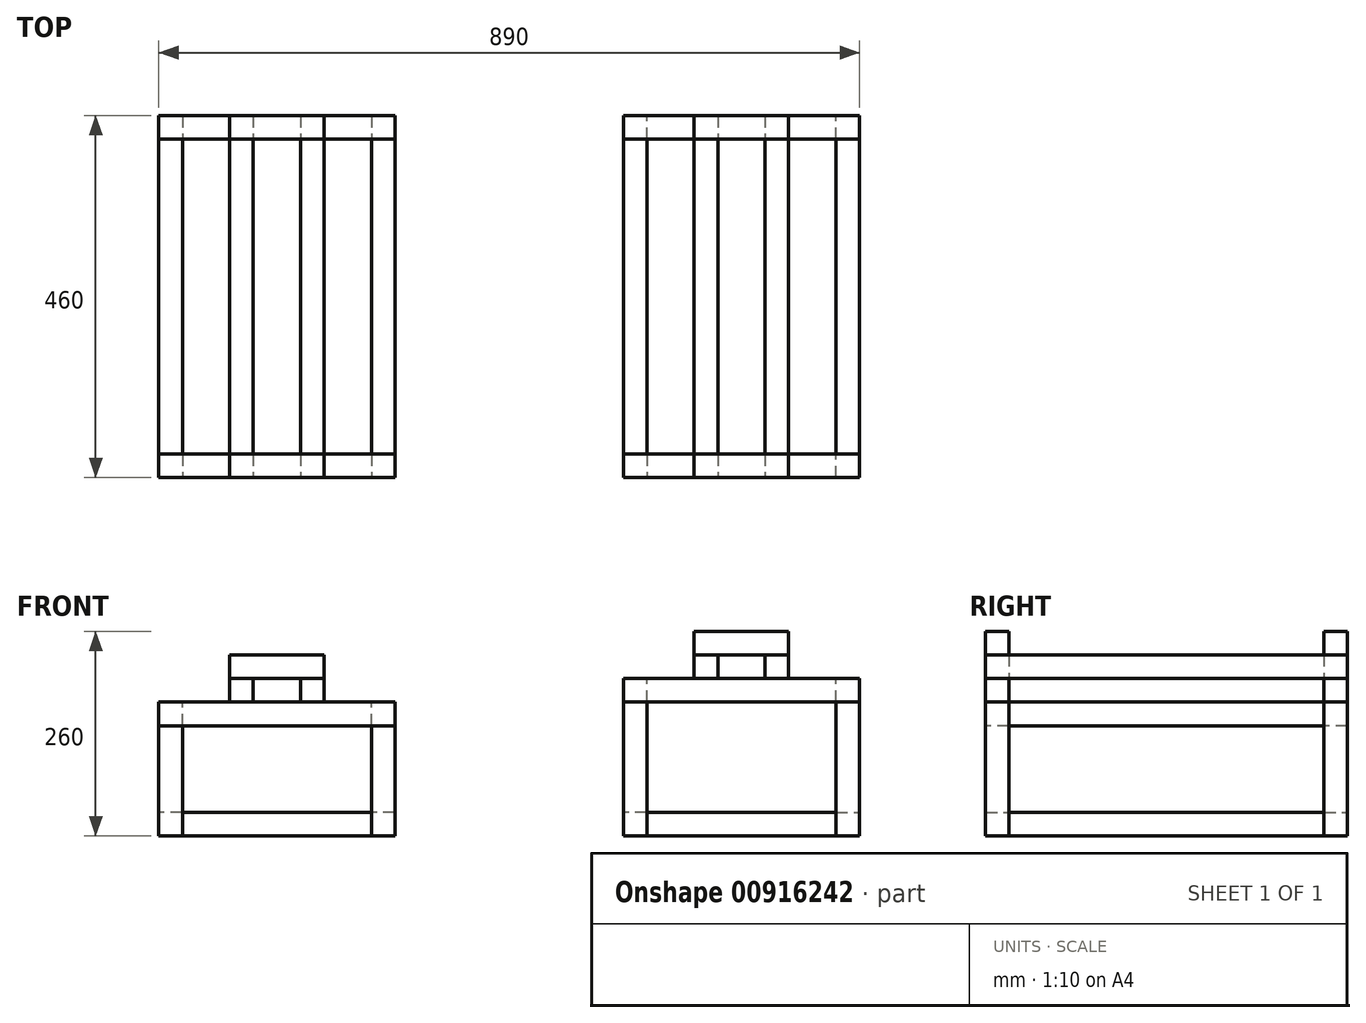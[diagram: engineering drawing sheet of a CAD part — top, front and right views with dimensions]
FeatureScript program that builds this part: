
annotation { "Feature Type Name" : "Feature", "Feature Type Description" : "" }
export const myFeature = defineFeature(function(context is Context, id is Id, definition is map)
    precondition{}
    {
        {
            var Q0;
            Q0=qCreatedBy(makeId("Top.planeOp"),FACE);
            cPlane(context, id + "F0", {"entities" : qUnion([Q0]), "cplaneType" : CPlaneType.OFFSET, "offset" : 200 * mm, "width" : 150 * mm, "height" : 150 * mm});
        }
        {
            var Q0;
            Q0=qCreatedBy(id+"F0.planeOp",FACE);
            var sketch = newSketch(context, id + "F1", { "sketchPlane" : qUnion([Q0])});
            skLineSegment(sketch, "E0.bottom", {"start": v(-295, 145) * mm, "end": v(295, 145) * mm, "construction": true});
            skLineSegment(sketch, "E0.top", {"start": v(-295, -145) * mm, "end": v(295, -145) * mm, "construction": true});
            skLineSegment(sketch, "E0.left", {"start": v(-295, 145) * mm, "end": v(-295, -145) * mm, "construction": true});
            skLineSegment(sketch, "E0.right", {"start": v(295, 145) * mm, "end": v(295, -145) * mm, "construction": true});
            skLineSegment(sketch, "E1", {"start": v(-82.1, 0) * mm, "end": v(82.1, 0) * mm, "construction": true});
            skLineSegment(sketch, "E2", {"start": v(0, 92.7) * mm, "end": v(0, -92.7) * mm, "construction": true});
            skLineSegment(sketch, "E3.bottom", {"start": v(-265, 230) * mm, "end": v(-235, 230) * mm});
            skLineSegment(sketch, "E3.top", {"start": v(-265, -230) * mm, "end": v(-235, -230) * mm});
            skLineSegment(sketch, "E3.left", {"start": v(-265, 230) * mm, "end": v(-265, -230) * mm});
            skLineSegment(sketch, "E3.right", {"start": v(-235, 230) * mm, "end": v(-235, -230) * mm});
            skLineSegment(sketch, "E4.bottom", {"start": v(-355, 230) * mm, "end": v(-325, 230) * mm});
            skLineSegment(sketch, "E4.top", {"start": v(-355, -230) * mm, "end": v(-325, -230) * mm});
            skLineSegment(sketch, "E4.left", {"start": v(-355, 230) * mm, "end": v(-355, -230) * mm});
            skLineSegment(sketch, "E4.right", {"start": v(-325, 230) * mm, "end": v(-325, -230) * mm});
            skLineSegment(sketch, "E5.bottom", {"start": v(235, 230) * mm, "end": v(265, 230) * mm});
            skLineSegment(sketch, "E5.top", {"start": v(235, -230) * mm, "end": v(265, -230) * mm});
            skLineSegment(sketch, "E5.left", {"start": v(235, 230) * mm, "end": v(235, -230) * mm});
            skLineSegment(sketch, "E5.right", {"start": v(265, 230) * mm, "end": v(265, -230) * mm});
            skLineSegment(sketch, "E6.bottom", {"start": v(325, 230) * mm, "end": v(355, 230) * mm});
            skLineSegment(sketch, "E6.top", {"start": v(325, -230) * mm, "end": v(355, -230) * mm});
            skLineSegment(sketch, "E6.left", {"start": v(325, 230) * mm, "end": v(325, -230) * mm});
            skLineSegment(sketch, "E6.right", {"start": v(355, 230) * mm, "end": v(355, -230) * mm});
            skLineSegment(sketch, "E7", {"start": v(-325, -230) * mm, "end": v(-265, -230) * mm, "construction": true});
            skLineSegment(sketch, "E8", {"start": v(265, -230) * mm, "end": v(325, -230) * mm, "construction": true});
            skSolve(sketch);
        }
        {
            var Q0;
            Q0 = qSketchRegion(id + "F1", true);
            extrude(context, id + "F2", {"entities" : qUnion([Q0]), "oppositeDirection" : true, "depth" : 30 * mm, "offsetDistance" : 25 * mm});
        }
        {
            var Q0;
            Q0=makeQuery(id+"F2.opExtrude","SWEPT_BODY",BODY,{"disambiguationData":[OSD([sQuery(id+"F1.wireOp",EDGE,"E5.bottom"),sQuery(id+"F1.wireOp",EDGE,"E5.top"),sQuery(id+"F1.wireOp",EDGE,"E5.left"),sQuery(id+"F1.wireOp",EDGE,"E5.right")])]});
            var Q1;
            Q1=makeQuery(id+"F2.opExtrude","SWEPT_BODY",BODY,{"disambiguationData":[OSD([sQuery(id+"F1.wireOp",EDGE,"E6.bottom"),sQuery(id+"F1.wireOp",EDGE,"E6.top"),sQuery(id+"F1.wireOp",EDGE,"E6.left"),sQuery(id+"F1.wireOp",EDGE,"E6.right")])]});
            transform(context, id + "F3", {"entities" : qUnion([Q0, Q1]), "transformType" : TransformType.TRANSLATION_3D, "dx" : 0 * mm, "dy" : 0 * mm, "dz" : 30 * mm, "makeCopy" : false});
        }
        {
            var Q0;
            Q0=makeQuery(id+"F2.opExtrude","CAP_FACE",FACE,{"disambiguationData":[OSD([sQuery(id+"F1.wireOp",EDGE,"E4.bottom"),sQuery(id+"F1.wireOp",EDGE,"E4.top"),sQuery(id+"F1.wireOp",EDGE,"E4.left"),sQuery(id+"F1.wireOp",EDGE,"E4.right")])],"isStart":false});
            var sketch = newSketch(context, id + "F4", { "sketchPlane" : qUnion([Q0])});
            skLineSegment(sketch, "E9.bottom", {"start": v(-445, 230) * mm, "end": v(-145, 230) * mm});
            skLineSegment(sketch, "E9.top", {"start": v(-445, 200) * mm, "end": v(-145, 200) * mm});
            skLineSegment(sketch, "E9.left", {"start": v(-445, 230) * mm, "end": v(-445, 200) * mm});
            skLineSegment(sketch, "E9.right", {"start": v(-145, 230) * mm, "end": v(-145, 200) * mm});
            skLineSegment(sketch, "E10.bottom", {"start": v(-445, -230) * mm, "end": v(-145, -230) * mm});
            skLineSegment(sketch, "E10.top", {"start": v(-445, -200) * mm, "end": v(-145, -200) * mm});
            skLineSegment(sketch, "E10.left", {"start": v(-445, -230) * mm, "end": v(-445, -200) * mm});
            skLineSegment(sketch, "E10.right", {"start": v(-145, -230) * mm, "end": v(-145, -200) * mm});
            skLineSegment(sketch, "E11", {"start": v(-445, 42.3) * mm, "end": v(-355, 42.3) * mm, "construction": true});
            skLineSegment(sketch, "E12", {"start": v(-145, 36.39) * mm, "end": v(-235, 36.39) * mm, "construction": true});
            skSolve(sketch);
        }
        {
            var Q0;
            Q0 = qSketchRegion(id + "F4", true);
            extrude(context, id + "F5", {"entities" : qUnion([Q0]), "depth" : 30 * mm, "offsetDistance" : 25 * mm});
        }
        {
            var Q0;
            Q0=qCreatedBy(makeId("Top.planeOp"),FACE);
            var sketch = newSketch(context, id + "F6", { "sketchPlane" : qUnion([Q0])});
            skLineSegment(sketch, "E13.bottom", {"start": v(-175, -230) * mm, "end": v(-145, -230) * mm});
            skLineSegment(sketch, "E13.top", {"start": v(-175, -200) * mm, "end": v(-145, -200) * mm});
            skLineSegment(sketch, "E13.left", {"start": v(-175, -230) * mm, "end": v(-175, -200) * mm});
            skLineSegment(sketch, "E13.right", {"start": v(-145, -230) * mm, "end": v(-145, -200) * mm});
            skLineSegment(sketch, "E14.bottom", {"start": v(-175, 200) * mm, "end": v(-145, 200) * mm});
            skLineSegment(sketch, "E14.top", {"start": v(-175, 230) * mm, "end": v(-145, 230) * mm});
            skLineSegment(sketch, "E14.left", {"start": v(-175, 200) * mm, "end": v(-175, 230) * mm});
            skLineSegment(sketch, "E14.right", {"start": v(-145, 200) * mm, "end": v(-145, 230) * mm});
            skLineSegment(sketch, "E15.bottom", {"start": v(-445, -230) * mm, "end": v(-415, -230) * mm});
            skLineSegment(sketch, "E15.top", {"start": v(-445, -200) * mm, "end": v(-415, -200) * mm});
            skLineSegment(sketch, "E15.left", {"start": v(-445, -230) * mm, "end": v(-445, -200) * mm});
            skLineSegment(sketch, "E15.right", {"start": v(-415, -230) * mm, "end": v(-415, -200) * mm});
            skLineSegment(sketch, "E16.bottom", {"start": v(-445, 200) * mm, "end": v(-415, 200) * mm});
            skLineSegment(sketch, "E16.top", {"start": v(-445, 230) * mm, "end": v(-415, 230) * mm});
            skLineSegment(sketch, "E16.left", {"start": v(-445, 200) * mm, "end": v(-445, 230) * mm});
            skLineSegment(sketch, "E16.right", {"start": v(-415, 200) * mm, "end": v(-415, 230) * mm});
            skSolve(sketch);
        }
        {
            var Q0;
            Q0 = qSketchRegion(id + "F6", true);
            extrude(context, id + "F7", {"entities" : qUnion([Q0]), "endBound" : BoundingType.UP_TO_NEXT, "depth" : 25 * mm, "offsetDistance" : 25 * mm});
        }
        {
            var Q0;
            Q0=makeQuery(id+"F7.opExtrude","SWEPT_FACE",FACE,{"disambiguationData":[OSD([sQuery(id+"F6.wireOp",EDGE,"E15.right")])]});
            var sketch = newSketch(context, id + "F8", { "sketchPlane" : qUnion([Q0])});
            skLineSegment(sketch, "E17.bottom", {"start": v(-200, 0) * mm, "end": v(-230, 0) * mm});
            skLineSegment(sketch, "E17.top", {"start": v(-200, 30) * mm, "end": v(-230, 30) * mm});
            skLineSegment(sketch, "E17.left", {"start": v(-200, 0) * mm, "end": v(-200, 30) * mm});
            skLineSegment(sketch, "E17.right", {"start": v(-230, 0) * mm, "end": v(-230, 30) * mm});
            skLineSegment(sketch, "E18.bottom", {"start": v(230, 0) * mm, "end": v(200, 0) * mm});
            skLineSegment(sketch, "E18.top", {"start": v(230, 30) * mm, "end": v(200, 30) * mm});
            skLineSegment(sketch, "E18.left", {"start": v(230, 0) * mm, "end": v(230, 30) * mm});
            skLineSegment(sketch, "E18.right", {"start": v(200, 0) * mm, "end": v(200, 30) * mm});
            skSolve(sketch);
        }
        {
            var Q0;
            Q0 = qSketchRegion(id + "F8", true);
            extrude(context, id + "F9", {"entities" : qUnion([Q0]), "endBound" : BoundingType.UP_TO_NEXT, "depth" : 25 * mm, "offsetDistance" : 25 * mm});
        }
        {
            var Q0;
            Q0=makeQuery(id+"F7.opExtrude","SWEPT_FACE",FACE,{"disambiguationData":[OSD([sQuery(id+"F6.wireOp",EDGE,"E16.bottom")])]});
            var sketch = newSketch(context, id + "F10", { "sketchPlane" : qUnion([Q0])});
            skLineSegment(sketch, "E19.bottom", {"start": v(-445, 0) * mm, "end": v(-415, 0) * mm});
            skLineSegment(sketch, "E19.top", {"start": v(-445, 30) * mm, "end": v(-415, 30) * mm});
            skLineSegment(sketch, "E19.left", {"start": v(-445, 0) * mm, "end": v(-445, 30) * mm});
            skLineSegment(sketch, "E19.right", {"start": v(-415, 0) * mm, "end": v(-415, 30) * mm});
            skLineSegment(sketch, "E20.bottom", {"start": v(-175, 0) * mm, "end": v(-145, 0) * mm});
            skLineSegment(sketch, "E20.top", {"start": v(-175, 30) * mm, "end": v(-145, 30) * mm});
            skLineSegment(sketch, "E20.left", {"start": v(-175, 0) * mm, "end": v(-175, 30) * mm});
            skLineSegment(sketch, "E20.right", {"start": v(-145, 0) * mm, "end": v(-145, 30) * mm});
            skLineSegment(sketch, "E21.bottom", {"start": v(-445, 140) * mm, "end": v(-415, 140) * mm});
            skLineSegment(sketch, "E21.top", {"start": v(-445, 170) * mm, "end": v(-415, 170) * mm});
            skLineSegment(sketch, "E21.left", {"start": v(-445, 140) * mm, "end": v(-445, 170) * mm});
            skLineSegment(sketch, "E21.right", {"start": v(-415, 140) * mm, "end": v(-415, 170) * mm});
            skLineSegment(sketch, "E22.bottom", {"start": v(-175, 140) * mm, "end": v(-145, 140) * mm});
            skLineSegment(sketch, "E22.top", {"start": v(-175, 170) * mm, "end": v(-145, 170) * mm});
            skLineSegment(sketch, "E22.left", {"start": v(-175, 140) * mm, "end": v(-175, 170) * mm});
            skLineSegment(sketch, "E22.right", {"start": v(-145, 140) * mm, "end": v(-145, 170) * mm});
            skSolve(sketch);
        }
        {
            var Q0;
            Q0 = qSketchRegion(id + "F10", true);
            extrude(context, id + "F11", {"entities" : qUnion([Q0]), "endBound" : BoundingType.UP_TO_NEXT, "depth" : 25 * mm, "offsetDistance" : 25 * mm});
        }
        {
            var Q0;
            Q0=makeQuery(id+"F2.opExtrude","CAP_FACE",FACE,{"disambiguationData":[OSD([sQuery(id+"F1.wireOp",EDGE,"E4.bottom"),sQuery(id+"F1.wireOp",EDGE,"E4.top"),sQuery(id+"F1.wireOp",EDGE,"E4.left"),sQuery(id+"F1.wireOp",EDGE,"E4.right")])],"isStart":true});
            var sketch = newSketch(context, id + "F12", { "sketchPlane" : qUnion([Q0])});
            skLineSegment(sketch, "E23.bottom", {"start": v(-355, -200) * mm, "end": v(-235, -200) * mm});
            skLineSegment(sketch, "E23.top", {"start": v(-355, -230) * mm, "end": v(-235, -230) * mm});
            skLineSegment(sketch, "E23.left", {"start": v(-355, -200) * mm, "end": v(-355, -230) * mm});
            skLineSegment(sketch, "E23.right", {"start": v(-235, -200) * mm, "end": v(-235, -230) * mm});
            skLineSegment(sketch, "E24.bottom", {"start": v(-355, 230) * mm, "end": v(-235, 230) * mm});
            skLineSegment(sketch, "E24.top", {"start": v(-355, 200) * mm, "end": v(-235, 200) * mm});
            skLineSegment(sketch, "E24.left", {"start": v(-355, 230) * mm, "end": v(-355, 200) * mm});
            skLineSegment(sketch, "E24.right", {"start": v(-235, 230) * mm, "end": v(-235, 200) * mm});
            skLineSegment(sketch, "E25", {"start": v(0, 0) * mm, "end": v(-485.51, 0) * mm, "construction": true});
            skPoint(sketch, "E25.endSnap0", {"position": v(-355, 0) * mm});
            skSolve(sketch);
        }
        {
            var Q0;
            Q0 = qSketchRegion(id + "F12", true);
            extrude(context, id + "F13", {"entities" : qUnion([Q0]), "depth" : 30 * mm, "offsetDistance" : 25 * mm});
        }
        {
            var Q0;
            Q0=makeQuery(id+"F2.opExtrude","CAP_FACE",FACE,{"disambiguationData":[OSD([sQuery(id+"F1.wireOp",EDGE,"E5.bottom"),sQuery(id+"F1.wireOp",EDGE,"E5.top"),sQuery(id+"F1.wireOp",EDGE,"E5.left"),sQuery(id+"F1.wireOp",EDGE,"E5.right")])],"isStart":false});
            var sketch = newSketch(context, id + "F14", { "sketchPlane" : qUnion([Q0])});
            skLineSegment(sketch, "E26.bottom", {"start": v(145, 230) * mm, "end": v(445, 230) * mm});
            skLineSegment(sketch, "E26.top", {"start": v(145, 200) * mm, "end": v(445, 200) * mm});
            skLineSegment(sketch, "E26.left", {"start": v(145, 230) * mm, "end": v(145, 200) * mm});
            skLineSegment(sketch, "E26.right", {"start": v(445, 230) * mm, "end": v(445, 200) * mm});
            skLineSegment(sketch, "E27.bottom", {"start": v(145, -230) * mm, "end": v(445, -230) * mm});
            skLineSegment(sketch, "E27.top", {"start": v(145, -200) * mm, "end": v(445, -200) * mm});
            skLineSegment(sketch, "E27.left", {"start": v(145, -230) * mm, "end": v(145, -200) * mm});
            skLineSegment(sketch, "E27.right", {"start": v(445, -230) * mm, "end": v(445, -200) * mm});
            skLineSegment(sketch, "E28", {"start": v(445, 0) * mm, "end": v(355, 0) * mm, "construction": true});
            skLineSegment(sketch, "E29", {"start": v(145, 0) * mm, "end": v(235, 0) * mm, "construction": true});
            skSolve(sketch);
        }
        {
            var Q0;
            Q0 = qSketchRegion(id + "F14", true);
            extrude(context, id + "F15", {"entities" : qUnion([Q0]), "depth" : 30 * mm, "offsetDistance" : 25 * mm});
        }
        {
            var Q0;
            Q0=qCreatedBy(makeId("Top.planeOp"),FACE);
            var sketch = newSketch(context, id + "F16", { "sketchPlane" : qUnion([Q0])});
            skLineSegment(sketch, "E30.bottom", {"start": v(145, -230) * mm, "end": v(175, -230) * mm});
            skLineSegment(sketch, "E30.top", {"start": v(145, -200) * mm, "end": v(175, -200) * mm});
            skLineSegment(sketch, "E30.left", {"start": v(145, -230) * mm, "end": v(145, -200) * mm});
            skLineSegment(sketch, "E30.right", {"start": v(175, -230) * mm, "end": v(175, -200) * mm});
            skLineSegment(sketch, "E31.bottom", {"start": v(415, -200) * mm, "end": v(445, -200) * mm});
            skLineSegment(sketch, "E31.top", {"start": v(415, -230) * mm, "end": v(445, -230) * mm});
            skLineSegment(sketch, "E31.left", {"start": v(415, -200) * mm, "end": v(415, -230) * mm});
            skLineSegment(sketch, "E31.right", {"start": v(445, -200) * mm, "end": v(445, -230) * mm});
            skLineSegment(sketch, "E32.bottom", {"start": v(415, 230) * mm, "end": v(445, 230) * mm});
            skLineSegment(sketch, "E32.top", {"start": v(415, 200) * mm, "end": v(445, 200) * mm});
            skLineSegment(sketch, "E32.left", {"start": v(415, 230) * mm, "end": v(415, 200) * mm});
            skLineSegment(sketch, "E32.right", {"start": v(445, 230) * mm, "end": v(445, 200) * mm});
            skLineSegment(sketch, "E33.bottom", {"start": v(175, 230) * mm, "end": v(145, 230) * mm});
            skLineSegment(sketch, "E33.top", {"start": v(175, 200) * mm, "end": v(145, 200) * mm});
            skLineSegment(sketch, "E33.left", {"start": v(175, 230) * mm, "end": v(175, 200) * mm});
            skLineSegment(sketch, "E33.right", {"start": v(145, 230) * mm, "end": v(145, 200) * mm});
            skSolve(sketch);
        }
        {
            var Q0;
            Q0 = qSketchRegion(id + "F16", true);
            extrude(context, id + "F17", {"entities" : qUnion([Q0]), "endBound" : BoundingType.UP_TO_NEXT, "depth" : 25 * mm, "offsetDistance" : 25 * mm});
        }
        {
            var Q0;
            Q0=makeQuery(id+"F17.opExtrude","SWEPT_FACE",FACE,{"disambiguationData":[OSD([sQuery(id+"F16.wireOp",EDGE,"E30.right")])]});
            var sketch = newSketch(context, id + "F18", { "sketchPlane" : qUnion([Q0])});
            skLineSegment(sketch, "E34.bottom", {"start": v(-200, 0) * mm, "end": v(-230, 0) * mm});
            skLineSegment(sketch, "E34.top", {"start": v(-200, 30) * mm, "end": v(-230, 30) * mm});
            skLineSegment(sketch, "E34.left", {"start": v(-200, 0) * mm, "end": v(-200, 30) * mm});
            skLineSegment(sketch, "E34.right", {"start": v(-230, 0) * mm, "end": v(-230, 30) * mm});
            skLineSegment(sketch, "E35.bottom", {"start": v(200, 0) * mm, "end": v(230, 0) * mm});
            skLineSegment(sketch, "E35.top", {"start": v(200, 30) * mm, "end": v(230, 30) * mm});
            skLineSegment(sketch, "E35.left", {"start": v(200, 0) * mm, "end": v(200, 30) * mm});
            skLineSegment(sketch, "E35.right", {"start": v(230, 0) * mm, "end": v(230, 30) * mm});
            skSolve(sketch);
        }
        {
            var Q0;
            Q0 = qSketchRegion(id + "F18", true);
            extrude(context, id + "F19", {"entities" : qUnion([Q0]), "endBound" : BoundingType.UP_TO_NEXT, "depth" : 25 * mm, "offsetDistance" : 25 * mm});
        }
        {
            var Q0;
            Q0=makeQuery(id+"F17.opExtrude","SWEPT_FACE",FACE,{"disambiguationData":[OSD([sQuery(id+"F16.wireOp",EDGE,"E30.top")])]});
            var sketch = newSketch(context, id + "F20", { "sketchPlane" : qUnion([Q0])});
            skLineSegment(sketch, "E36.bottom", {"start": v(-145, 0) * mm, "end": v(-175, 0) * mm});
            skLineSegment(sketch, "E36.top", {"start": v(-145, 30) * mm, "end": v(-175, 30) * mm});
            skLineSegment(sketch, "E36.left", {"start": v(-145, 0) * mm, "end": v(-145, 30) * mm});
            skLineSegment(sketch, "E36.right", {"start": v(-175, 0) * mm, "end": v(-175, 30) * mm});
            skLineSegment(sketch, "E37.bottom", {"start": v(-415, 0) * mm, "end": v(-445, 0) * mm});
            skLineSegment(sketch, "E37.top", {"start": v(-415, 30) * mm, "end": v(-445, 30) * mm});
            skLineSegment(sketch, "E37.left", {"start": v(-415, 0) * mm, "end": v(-415, 30) * mm});
            skLineSegment(sketch, "E37.right", {"start": v(-445, 0) * mm, "end": v(-445, 30) * mm});
            skLineSegment(sketch, "E38.bottom", {"start": v(-445, 200) * mm, "end": v(-415, 200) * mm});
            skLineSegment(sketch, "E38.top", {"start": v(-445, 170) * mm, "end": v(-415, 170) * mm});
            skLineSegment(sketch, "E38.left", {"start": v(-445, 200) * mm, "end": v(-445, 170) * mm});
            skLineSegment(sketch, "E38.right", {"start": v(-415, 200) * mm, "end": v(-415, 170) * mm});
            skPoint(sketch, "E39.oppositeSnap0", {"position": v(-160, 170) * mm});
            skLineSegment(sketch, "E39.bottom", {"start": v(-175, 200) * mm, "end": v(-145, 200) * mm});
            skLineSegment(sketch, "E39.top", {"start": v(-175, 170) * mm, "end": v(-145, 170) * mm});
            skLineSegment(sketch, "E39.left", {"start": v(-175, 200) * mm, "end": v(-175, 170) * mm});
            skLineSegment(sketch, "E39.right", {"start": v(-145, 200) * mm, "end": v(-145, 170) * mm});
            skSolve(sketch);
        }
        {
            var Q0;
            Q0 = qSketchRegion(id + "F20", true);
            extrude(context, id + "F21", {"entities" : qUnion([Q0]), "endBound" : BoundingType.UP_TO_NEXT, "depth" : 25 * mm, "offsetDistance" : 25 * mm});
        }
        {
            var Q0;
            Q0=makeQuery(id+"F2.opExtrude","CAP_FACE",FACE,{"disambiguationData":[OSD([sQuery(id+"F1.wireOp",EDGE,"E5.bottom"),sQuery(id+"F1.wireOp",EDGE,"E5.top"),sQuery(id+"F1.wireOp",EDGE,"E5.left"),sQuery(id+"F1.wireOp",EDGE,"E5.right")])],"isStart":true});
            var sketch = newSketch(context, id + "F22", { "sketchPlane" : qUnion([Q0])});
            skLineSegment(sketch, "E40.bottom", {"start": v(235, 230) * mm, "end": v(355, 230) * mm});
            skLineSegment(sketch, "E40.top", {"start": v(235, 200) * mm, "end": v(355, 200) * mm});
            skLineSegment(sketch, "E40.left", {"start": v(235, 230) * mm, "end": v(235, 200) * mm});
            skLineSegment(sketch, "E40.right", {"start": v(355, 230) * mm, "end": v(355, 200) * mm});
            skLineSegment(sketch, "E41.bottom", {"start": v(235, -230) * mm, "end": v(355, -230) * mm});
            skLineSegment(sketch, "E41.top", {"start": v(235, -200) * mm, "end": v(355, -200) * mm});
            skLineSegment(sketch, "E41.left", {"start": v(235, -230) * mm, "end": v(235, -200) * mm});
            skLineSegment(sketch, "E41.right", {"start": v(355, -230) * mm, "end": v(355, -200) * mm});
            skSolve(sketch);
        }
        {
            var Q0;
            Q0 = qSketchRegion(id + "F22", true);
            extrude(context, id + "F23", {"entities" : qUnion([Q0]), "depth" : 30 * mm, "offsetDistance" : 25 * mm});
        }
    });
